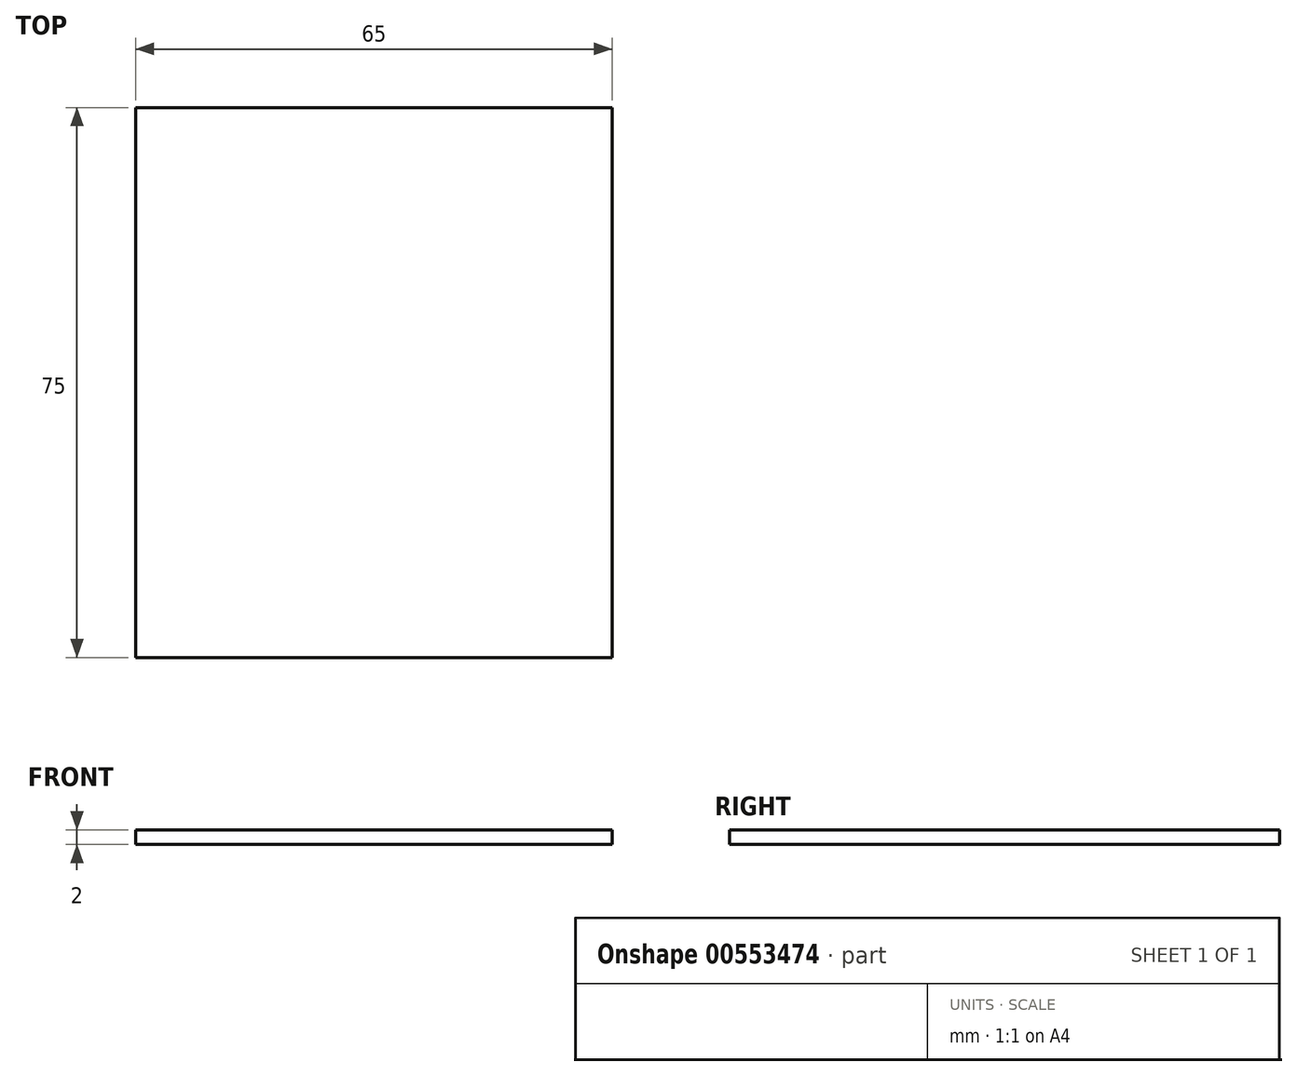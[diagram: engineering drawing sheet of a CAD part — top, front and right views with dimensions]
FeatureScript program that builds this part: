
annotation { "Feature Type Name" : "Feature", "Feature Type Description" : "" }
export const myFeature = defineFeature(function(context is Context, id is Id, definition is map)
    precondition{}
    {
        {
            var Q0;
            Q0=qCreatedBy(makeId("Top.planeOp"),FACE);
            var sketch = newSketch(context, id + "F0", { "sketchPlane" : qUnion([Q0])});
            skLineSegment(sketch, "E0.bottom", {"start": v(-32.5, 37.5) * mm, "end": v(32.5, 37.5) * mm});
            skLineSegment(sketch, "E0.top", {"start": v(-32.5, -37.5) * mm, "end": v(32.5, -37.5) * mm});
            skLineSegment(sketch, "E0.left", {"start": v(-32.5, 37.5) * mm, "end": v(-32.5, -37.5) * mm});
            skLineSegment(sketch, "E0.right", {"start": v(32.5, 37.5) * mm, "end": v(32.5, -37.5) * mm});
            skPoint(sketch, "E0.middle", {"position": v(0, 0) * mm});
            skSolve(sketch);
        }
        {
            var Q0;
            Q0=makeQuery(id+"F0.imprint","IMPRINT",FACE,{"disambiguationData":[TD([[makeQuery(id+"F0.imprint","IMPRINT",EDGE,{"derivedFrom":sQuery(id+"F0.wireOp",EDGE,"E0.bottom")}),-1.0]])]});
            extrude(context, id + "F1", {"entities" : qUnion([Q0]), "depth" : 2 * mm, "offsetDistance" : 25 * mm});
        }
    });
